# Revit family: QF_BPRO_CEK 58-58_574893
name_source: partatom
category: Sonderausstattung
revit_build: Autodesk Revit 2018 (Build: 20190510_1515(x64)
units: mm (PartAtom-declared; Revit-internal decimal feet)

## family parameters
Arbeitsebenenbasiert = Nein
Beim Laden mit Abzugskörper schneiden = Nein
Bemaßung runder Anschluss = Durchmesser verwenden
Gemeinsam genutzt = Nein
Immer vertikal = Ja
Raumberechnungspunkt = Ja
Teiletyp = Normal

## types (1)
- CEK 58-58
    Abdeckhaube Höhe = 179 mm  [stored 0.58727 ft]
    Abdeckhaube Länge = 625 mm  [stored 2.05052 ft]
    Abdeckhaube Tiefe = 625 mm  [stored 2.05052 ft]
    Artikel Nummer = 574893
    Beschreibung = Bühnenspender mit Kühlschlitzen;
zum Einfahren und Kühlen von Geschirr in Kühlräumen;
Plattform 581 x 581 mm
    Beschreibung durch Hersteller analog Leistungsverzeichniskurztext = Abmessungen

Länge:					  805 mm
Breite:					  700 mm
Höhe:					  911 mm
Höhe (mit Option Abdeckhaube):		1079 mm
Arbeitshöhe:					  900 mm



Ausführung

Aufbau
Der Bühnenspender besteht komplett aus CNS 18/10. Die Oberfläche ist mikroliert. 
Die Plattform dient zur Aufnahme unterschiedlicher Geschirrarten. Der Korpus ist einwandig und mit Kühlschlitzen versehen zum kühlen von Geschirr in Kühlräumen.
Der Bühnenspender hat eine durchgehende pulverbeschichtete Innenverkleidung, um das Rutschen des Geschirrs und somit Beschädigungen an der Innenseite des Korpus zu vermeiden.
Durch Ein- bzw. Aushängen der Zugfedern kann die Federspannung entsprechend dem Stapelgut reguliert werden, um eine gleichbleibende Ausgabehöhe zu gewährleisten.
Bedienseitig ist ein CNS-Sicherheits-Schiebegriff mit seitlichen Stoßschutzelementen aus Kunststoff (Polyamid) angebracht.
Fahrbar ist der Spender mittels rostfreien Kunststoffrollen (4 Lenkrollen, 2 mit Feststeller mit 125 mm ø). Massive Stoßecken aus Kunststoff (Polyamid) an allen vier Ecken schützen vor Beschädigung.


Zubehör/Optionen

•	Abdeckhaube (625 x 625 mm), Polycarbonat
Stapelhöhe mit Abdeckhaube:	680 mm
Stapelhöhe ohne Abdeckhaube:	540 mm
•	     Weitere Zubehöre und Rollenausführungen siehe Gesamt-Preisliste


Technische Daten

Werkstoff:		CNS 18/10
Gewicht:		58 kg 
Kapazität:		abhängig von Geschirrart
Lichtes Maß:		581 x 581 mm


Besonderheit

•	durchgehend pulverbeschichtete Innenverkleidung
•	Veränderung der Federspannung möglich
•	Korpus mit Kühlschlitzen
•	gemäß DIN 18665, Teil 6 


Fabrikat

Hersteller:			B.PRO
Modell:				CEK 58/ 55
Best.Nr.			574 893
    Beschreibung durch Hersteller analog Leistungsverzeichnislangtext = Abmessungen

Länge:					  805 mm
Breite:					  700 mm
Höhe:					  911 mm
Höhe (mit Option Abdeckhaube):		1079 mm
Arbeitshöhe:					  900 mm



Ausführung

Aufbau
Der Bühnenspender besteht komplett aus CNS 18/10. Die Oberfläche ist mikroliert. 
Die Plattform dient zur Aufnahme unterschiedlicher Geschirrarten. Der Korpus ist einwandig und mit Kühlschlitzen versehen zum kühlen von Geschirr in Kühlräumen.
Der Bühnenspender hat eine durchgehende pulverbeschichtete Innenverkleidung, um das Rutschen des Geschirrs und somit Beschädigungen an der Innenseite des Korpus zu vermeiden.
Durch Ein- bzw. Aushängen der Zugfedern kann die Federspannung entsprechend dem Stapelgut reguliert werden, um eine gleichbleibende Ausgabehöhe zu gewährleisten.
Bedienseitig ist ein CNS-Sicherheits-Schiebegriff mit seitlichen Stoßschutzelementen aus Kunststoff (Polyamid) angebracht.
Fahrbar ist der Spender mittels rostfreien Kunststoffrollen (4 Lenkrollen, 2 mit Feststeller mit 125 mm ø). Massive Stoßecken aus Kunststoff (Polyamid) an allen vier Ecken schützen vor Beschädigung.


Zubehör/Optionen

•	Abdeckhaube (625 x 625 mm), Polycarbonat
Stapelhöhe mit Abdeckhaube:	680 mm
Stapelhöhe ohne Abdeckhaube:	540 mm
•	     Weitere Zubehöre und Rollenausführungen siehe Gesamt-Preisliste


Technische Daten

Werkstoff:		CNS 18/10
Gewicht:		58 kg 
Kapazität:		abhängig von Geschirrart
Lichtes Maß:		581 x 581 mm


Besonderheit

•	durchgehend pulverbeschichtete Innenverkleidung
•	Veränderung der Federspannung möglich
•	Korpus mit Kühlschlitzen
•	gemäß DIN 18665, Teil 6 


Fabrikat

Hersteller:			B.PRO
Modell:				CEK 58/ 55
Best.Nr.			574 893
    Gerätegewicht Netto = 58.00 kg
    Großküchengerätezuordnung = Ja
    Hersteller = B.PRO GmbH
    Höhe Korpus = 900 mm  [stored 2.95276 ft]
    Internetadresse Gerätehersteller = https://www.bpro-solutions.com
    Internetadresse für Ersatzteilliste = https://www.bpro-solutions.com
    Kosten = 2273.6 $
    Länge Gerätebreite = 805 mm
    Länge Korpus = 700 mm  [stored 2.29659 ft]
    Material = QF_Metal-Stainless-Steel_general
    Material_Stoßschutz = QF_Rubber-Black-Matt
    Modell = CEK 58-58
    Plattform Länge = 581 mm  [stored 1.90617 ft]
    Plattform Tiefe = 581 mm  [stored 1.90617 ft]
    Schacht Tiefe = 600 mm
    Sockelhöhe = 161 mm  [stored 0.528215 ft]
    Tiefe = 700 mm  [stored 2.29659 ft]
    Tiefe Korpus = 630 mm  [stored 2.06693 ft]
    Typenkommentare = Bühnenspender mit Kühlschlitzen
    URL = https://www.bpro-solutions.com
    Warnhinweise = Ausführliche Gefahrenhinweise entnehmen Sie der Betriebsanleitung.
    Zubehör = Nein

note: [stored X ft] marks values corroborated as IEEE doubles in the binary element streams (Revit-internal decimal feet)
